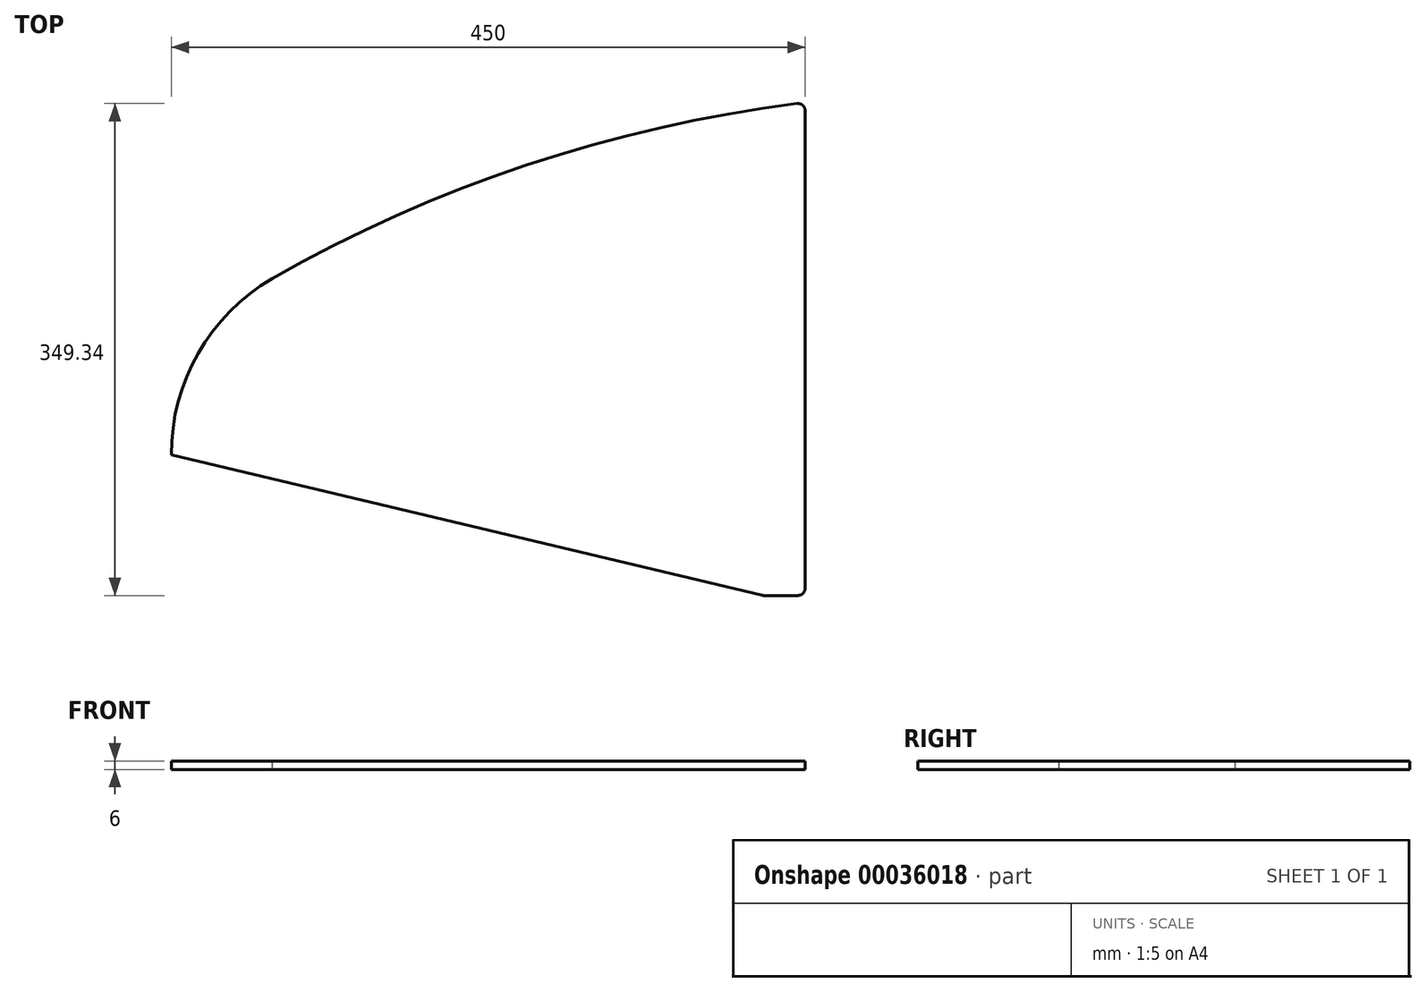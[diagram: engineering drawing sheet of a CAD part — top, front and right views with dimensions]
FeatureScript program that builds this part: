
annotation { "Feature Type Name" : "Feature", "Feature Type Description" : "" }
export const myFeature = defineFeature(function(context is Context, id is Id, definition is map)
    precondition{}
    {
        {
            var Q0;
            Q0=qCreatedBy(makeId("Top.planeOp"),FACE);
            var sketch = newSketch(context, id + "F0", { "sketchPlane" : qUnion([Q0])});
            skLineSegment(sketch, "E0.rect.bottom", {"start": v(225, -175) * mm, "end": v(-225, -175) * mm});
            skLineSegment(sketch, "E0.rect.top", {"start": v(225, 175) * mm, "end": v(-225, 175) * mm});
            skLineSegment(sketch, "E0.rect.left", {"start": v(225, -175) * mm, "end": v(225, 175) * mm});
            skLineSegment(sketch, "E0.rect.right", {"start": v(-225, -175) * mm, "end": v(-225, 175) * mm});
            skPoint(sketch, "E0.rect.middle", {"position": v(0, 0) * mm});
            skLineSegment(sketch, "E1", {"start": v(225, -175) * mm, "end": v(195, -175) * mm});
            skLineSegment(sketch, "E2", {"start": v(195, -175) * mm, "end": v(-225, -75) * mm});
            skLineSegment(sketch, "E3", {"start": v(-225, -75) * mm, "end": v(-225, -175) * mm});
            skArc(sketch, "E4", {"start": v(-153.57, 50.04) * mm, "mid": v(-205.88, -3) * mm, "end": v(-225, -75) * mm});
            skArc(sketch, "E5", {"start": v(225, 175) * mm, "mid": v(29.5, 131.36) * mm, "end": v(-153.57, 50.04) * mm});
            skSolve(sketch);
        }
        {
            var Q0;
            Q0=makeQuery(id+"F0.imprint","IMPRINT",FACE,{"disambiguationData":[TD([[makeQuery(id+"F0.imprint","IMPRINT",EDGE,{"derivedFrom":sQuery(id+"F0.wireOp",EDGE,"E0.rect.left")}),1.0]])]});
            extrude(context, id + "F1", {"entities" : qUnion([Q0]), "depth" : 6 * mm});
        }
        {
            var Q0;
            Q0=makeQuery(id+"F1.opExtrude","SWEPT_EDGE",EDGE,{"disambiguationData":[OSD([sQuery(id+"F0.wireOp",EDGE,"E0.rect.top"),sQuery(id+"F0.wireOp",EDGE,"E0.rect.left")])]});
            var Q1;
            Q1=makeQuery(id+"F1.opExtrude","SWEPT_EDGE",EDGE,{"disambiguationData":[OSD([sQuery(id+"F0.wireOp",EDGE,"E0.rect.bottom"),sQuery(id+"F0.wireOp",EDGE,"E0.rect.right")])]});
            fillet(context, id + "F2", {"entities" : qUnion([Q0, Q1]), "radius" : 5 * mm, "tangentPropagation" : true, "allowEdgeOverflow" : false});
        }
    });
